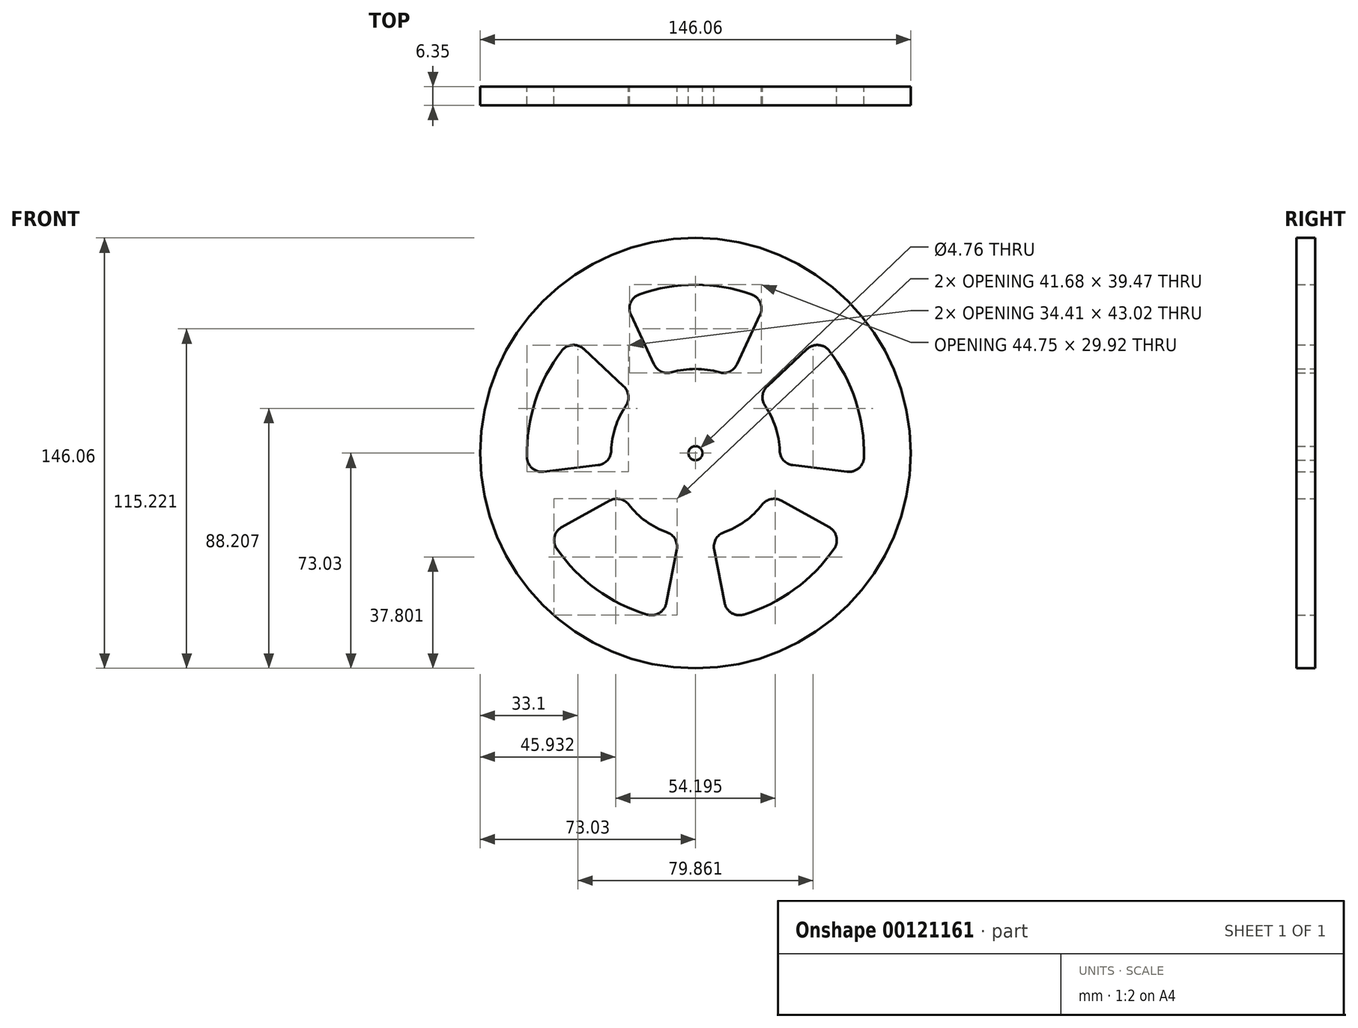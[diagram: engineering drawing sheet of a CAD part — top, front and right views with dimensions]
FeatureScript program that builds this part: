
annotation { "Feature Type Name" : "Feature", "Feature Type Description" : "" }
export const myFeature = defineFeature(function(context is Context, id is Id, definition is map)
    precondition{}
    {
        {
            var Q0;
            Q0=qCreatedBy(makeId("Front.planeOp"),FACE);
            var sketch = newSketch(context, id + "F0", { "sketchPlane" : qUnion([Q0])});
            skCircle(sketch, "E0", {"center": v(0, 0) * mm, "radius": 73.03 * mm});
            skCircle(sketch, "E1", {"center": v(0, 0) * mm, "radius": 2.38 * mm});
            skLineSegment(sketch, "E2", {"start": v(0, 0) * mm, "end": v(0, 73.03) * mm, "construction": true});
            skArc(sketch, "E3", {"start": v(24.15, 51.8) * mm, "mid": v(0, 57.15) * mm, "end": v(-24.15, 51.8) * mm});
            skArc(sketch, "E4", {"start": v(12.08, 25.9) * mm, "mid": v(0, 28.57) * mm, "end": v(-12.08, 25.9) * mm});
            skLineSegment(sketch, "E5", {"start": v(0, 0) * mm, "end": v(30.86, 66.18) * mm, "construction": true});
            skLineSegment(sketch, "E6.MirrorCS", {"start": v(0, 0) * mm, "end": v(-30.86, 66.18) * mm, "construction": true});
            skLineSegment(sketch, "E7", {"start": v(-24.15, 51.8) * mm, "end": v(-12.08, 25.9) * mm});
            skLineSegment(sketch, "E8", {"start": v(12.08, 25.9) * mm, "end": v(24.15, 51.8) * mm});
            skLineSegment(sketch, "E9.1.0", {"start": v(-20.9, 19.49) * mm, "end": v(-41.8, 38.98) * mm});
            skLineSegment(sketch, "E9.1.1", {"start": v(-56.72, -6.96) * mm, "end": v(-28.36, -3.48) * mm});
            skArc(sketch, "E9.1.2", {"start": v(-20.9, 19.49) * mm, "mid": v(-27.18, 8.83) * mm, "end": v(-28.36, -3.48) * mm});
            skArc(sketch, "E9.1.3", {"start": v(-41.8, 38.98) * mm, "mid": v(-54.35, 17.66) * mm, "end": v(-56.72, -6.96) * mm});
            skLineSegment(sketch, "E9.2.0", {"start": v(-25, -13.85) * mm, "end": v(-49.98, -27.7) * mm});
            skLineSegment(sketch, "E9.2.1", {"start": v(-10.9, -56.1) * mm, "end": v(-5.45, -28.05) * mm});
            skArc(sketch, "E9.2.2", {"start": v(-25, -13.85) * mm, "mid": v(-16.8, -23.12) * mm, "end": v(-5.45, -28.05) * mm});
            skArc(sketch, "E9.2.3", {"start": v(-49.98, -27.7) * mm, "mid": v(-33.6, -46.24) * mm, "end": v(-10.9, -56.1) * mm});
            skLineSegment(sketch, "E10.3.3.0", {"start": v(49.98, -27.7) * mm, "end": v(25, -13.85) * mm});
            skArc(sketch, "E10.6.3.0", {"start": v(5.45, -28.05) * mm, "mid": v(16.8, -23.12) * mm, "end": v(25, -13.85) * mm});
            skLineSegment(sketch, "E10.7.3.0", {"start": v(5.45, -28.05) * mm, "end": v(10.9, -56.1) * mm});
            skArc(sketch, "E10.10.3.0", {"start": v(10.9, -56.1) * mm, "mid": v(33.6, -46.24) * mm, "end": v(49.98, -27.7) * mm});
            skLineSegment(sketch, "E10.3.4.0", {"start": v(41.8, 38.98) * mm, "end": v(20.9, 19.49) * mm});
            skArc(sketch, "E10.6.4.0", {"start": v(28.36, -3.48) * mm, "mid": v(27.18, 8.83) * mm, "end": v(20.9, 19.49) * mm});
            skLineSegment(sketch, "E10.7.4.0", {"start": v(28.36, -3.48) * mm, "end": v(56.72, -6.96) * mm});
            skArc(sketch, "E10.10.4.0", {"start": v(56.72, -6.96) * mm, "mid": v(54.35, 17.66) * mm, "end": v(41.8, 38.98) * mm});
            skSolve(sketch);
        }
        {
            var Q0;
            Q0=makeQuery(id+"F0.imprint","IMPRINT",FACE,{"disambiguationData":[TD([[makeQuery(id+"F0.imprint","IMPRINT",EDGE,{"derivedFrom":sQuery(id+"F0.wireOp",EDGE,"E0")}),1.0]])]});
            extrude(context, id + "F1", {"entities" : qUnion([Q0]), "depth" : 6.35 * mm});
        }
        {
            var Q0;
            Q0=makeQuery(id+"F1.opExtrude","SWEPT_EDGE",EDGE,{"disambiguationData":[OSD([sQuery(id+"F0.wireOp",EDGE,"E4"),sQuery(id+"F0.wireOp",EDGE,"E8")])]});
            var Q1;
            Q1=makeQuery(id+"F1.opExtrude","SWEPT_EDGE",EDGE,{"disambiguationData":[OSD([sQuery(id+"F0.wireOp",EDGE,"E4"),sQuery(id+"F0.wireOp",EDGE,"E7")])]});
            var Q2;
            Q2=makeQuery(id+"F1.opExtrude","SWEPT_EDGE",EDGE,{"disambiguationData":[OSD([sQuery(id+"F0.wireOp",EDGE,"E9.1.0"),sQuery(id+"F0.wireOp",EDGE,"E9.1.2")])]});
            var Q3;
            Q3=makeQuery(id+"F1.opExtrude","SWEPT_EDGE",EDGE,{"disambiguationData":[OSD([sQuery(id+"F0.wireOp",EDGE,"E9.1.1"),sQuery(id+"F0.wireOp",EDGE,"E9.1.2")])]});
            var Q4;
            Q4=makeQuery(id+"F1.opExtrude","SWEPT_EDGE",EDGE,{"disambiguationData":[OSD([sQuery(id+"F0.wireOp",EDGE,"E9.2.0"),sQuery(id+"F0.wireOp",EDGE,"E9.2.2")])]});
            var Q5;
            Q5=makeQuery(id+"F1.opExtrude","SWEPT_EDGE",EDGE,{"disambiguationData":[OSD([sQuery(id+"F0.wireOp",EDGE,"E9.2.1"),sQuery(id+"F0.wireOp",EDGE,"E9.2.2")])]});
            var Q6;
            Q6=makeQuery(id+"F1.opExtrude","SWEPT_EDGE",EDGE,{"disambiguationData":[OSD([sQuery(id+"F0.wireOp",EDGE,"E10.6.3.0"),sQuery(id+"F0.wireOp",EDGE,"E10.7.3.0")])]});
            var Q7;
            Q7=makeQuery(id+"F1.opExtrude","SWEPT_EDGE",EDGE,{"disambiguationData":[OSD([sQuery(id+"F0.wireOp",EDGE,"E10.3.3.0"),sQuery(id+"F0.wireOp",EDGE,"E10.6.3.0")])]});
            var Q8;
            Q8=makeQuery(id+"F1.opExtrude","SWEPT_EDGE",EDGE,{"disambiguationData":[OSD([sQuery(id+"F0.wireOp",EDGE,"E10.6.4.0"),sQuery(id+"F0.wireOp",EDGE,"E10.7.4.0")])]});
            var Q9;
            Q9=makeQuery(id+"F1.opExtrude","SWEPT_EDGE",EDGE,{"disambiguationData":[OSD([sQuery(id+"F0.wireOp",EDGE,"E10.3.4.0"),sQuery(id+"F0.wireOp",EDGE,"E10.6.4.0")])]});
            var Q10;
            Q10=makeQuery(id+"F1.opExtrude","SWEPT_EDGE",EDGE,{"disambiguationData":[OSD([sQuery(id+"F0.wireOp",EDGE,"E3"),sQuery(id+"F0.wireOp",EDGE,"E7")])]});
            var Q11;
            Q11=makeQuery(id+"F1.opExtrude","SWEPT_EDGE",EDGE,{"disambiguationData":[OSD([sQuery(id+"F0.wireOp",EDGE,"E9.1.0"),sQuery(id+"F0.wireOp",EDGE,"E9.1.3")])]});
            var Q12;
            Q12=makeQuery(id+"F1.opExtrude","SWEPT_EDGE",EDGE,{"disambiguationData":[OSD([sQuery(id+"F0.wireOp",EDGE,"E9.1.1"),sQuery(id+"F0.wireOp",EDGE,"E9.1.3")])]});
            var Q13;
            Q13=makeQuery(id+"F1.opExtrude","SWEPT_EDGE",EDGE,{"disambiguationData":[OSD([sQuery(id+"F0.wireOp",EDGE,"E9.2.0"),sQuery(id+"F0.wireOp",EDGE,"E9.2.3")])]});
            var Q14;
            Q14=makeQuery(id+"F1.opExtrude","SWEPT_EDGE",EDGE,{"disambiguationData":[OSD([sQuery(id+"F0.wireOp",EDGE,"E9.2.1"),sQuery(id+"F0.wireOp",EDGE,"E9.2.3")])]});
            var Q15;
            Q15=makeQuery(id+"F1.opExtrude","SWEPT_EDGE",EDGE,{"disambiguationData":[OSD([sQuery(id+"F0.wireOp",EDGE,"E10.7.3.0"),sQuery(id+"F0.wireOp",EDGE,"E10.10.3.0")])]});
            var Q16;
            Q16=makeQuery(id+"F1.opExtrude","SWEPT_EDGE",EDGE,{"disambiguationData":[OSD([sQuery(id+"F0.wireOp",EDGE,"E10.3.3.0"),sQuery(id+"F0.wireOp",EDGE,"E10.10.3.0")])]});
            var Q17;
            Q17=makeQuery(id+"F1.opExtrude","SWEPT_EDGE",EDGE,{"disambiguationData":[OSD([sQuery(id+"F0.wireOp",EDGE,"E10.7.4.0"),sQuery(id+"F0.wireOp",EDGE,"E10.10.4.0")])]});
            var Q18;
            Q18=makeQuery(id+"F1.opExtrude","SWEPT_EDGE",EDGE,{"disambiguationData":[OSD([sQuery(id+"F0.wireOp",EDGE,"E10.3.4.0"),sQuery(id+"F0.wireOp",EDGE,"E10.10.4.0")])]});
            var Q19;
            Q19=makeQuery(id+"F1.opExtrude","SWEPT_EDGE",EDGE,{"disambiguationData":[OSD([sQuery(id+"F0.wireOp",EDGE,"E3"),sQuery(id+"F0.wireOp",EDGE,"E8")])]});
            fillet(context, id + "F2", {"entities" : qUnion([Q0, Q1, Q2, Q3, Q4, Q5, Q6, Q7, Q8, Q9, Q10, Q11, Q12, Q13, Q14, Q15, Q16, Q17, Q18, Q19]), "radius" : 5.08 * mm, "tangentPropagation" : true, "allowEdgeOverflow" : false});
        }
    });
